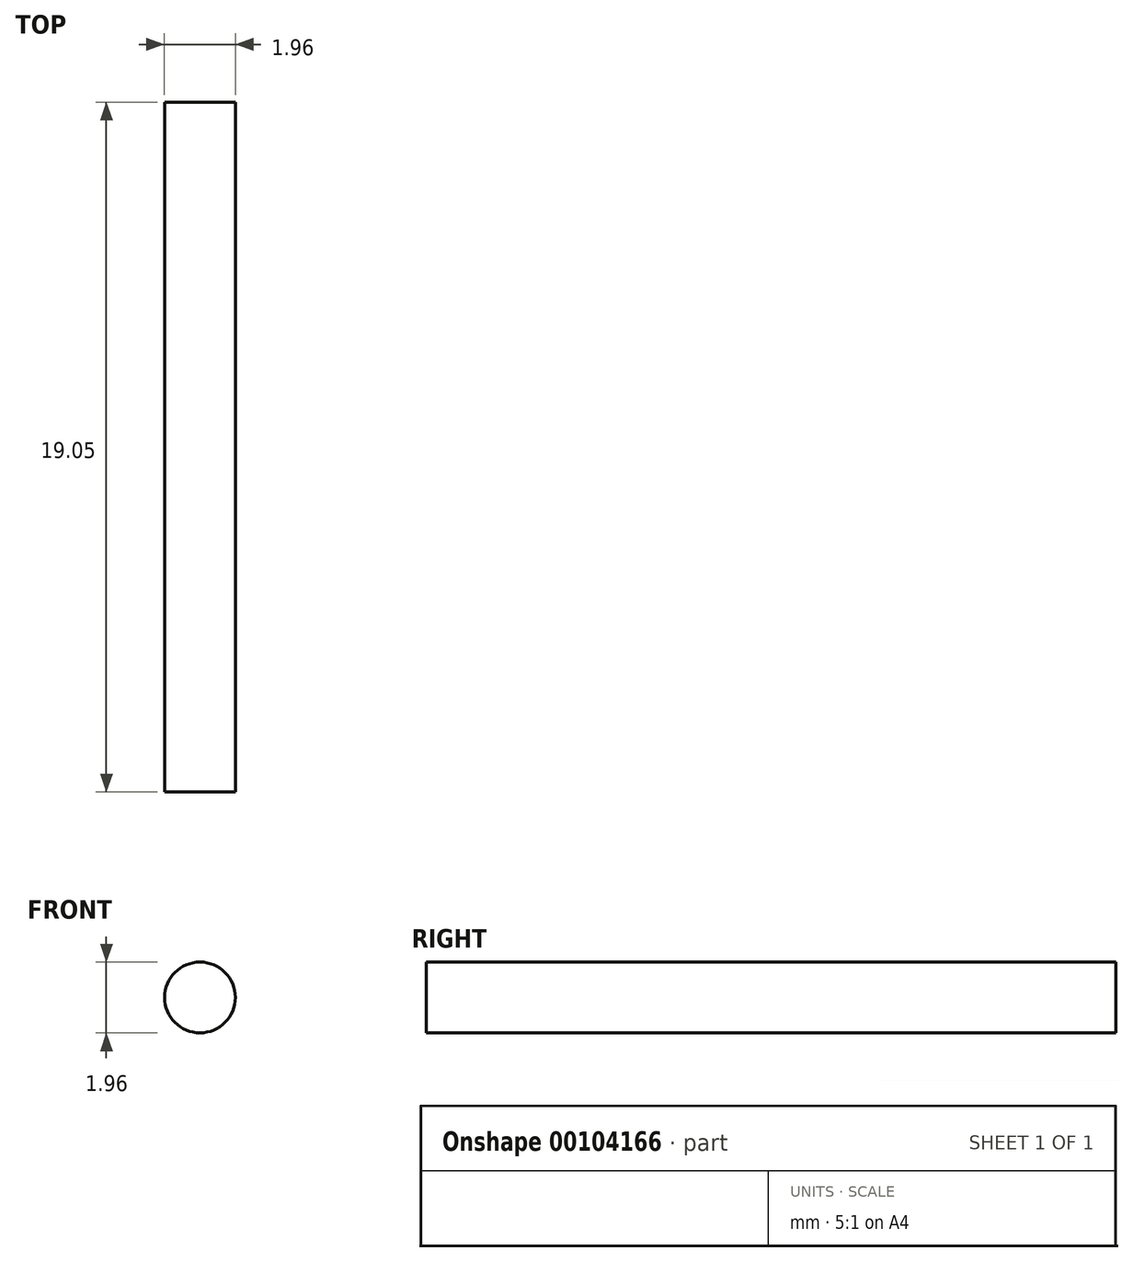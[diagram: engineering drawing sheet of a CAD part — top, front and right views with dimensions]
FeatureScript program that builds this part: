
annotation { "Feature Type Name" : "Feature", "Feature Type Description" : "" }
export const myFeature = defineFeature(function(context is Context, id is Id, definition is map)
    precondition{}
    {
        {
            var Q0;
            Q0=qCreatedBy(makeId("Front.planeOp"),FACE);
            var sketch = newSketch(context, id + "F0", { "sketchPlane" : qUnion([Q0])});
            skCircle(sketch, "E0", {"center": v(-44.55, 9.56) * mm, "radius": 0.98 * mm});
            skSolve(sketch);
        }
        {
            var Q0;
            Q0=makeQuery(id+"F0.imprint","IMPRINT",FACE,{"disambiguationData":[TD([[makeQuery(id+"F0.imprint","IMPRINT",EDGE,{"derivedFrom":sQuery(id+"F0.wireOp",EDGE,"E0")}),1.0]])]});
            extrude(context, id + "F1", {"entities" : qUnion([Q0]), "depth" : 19.05 * mm});
        }
    });
